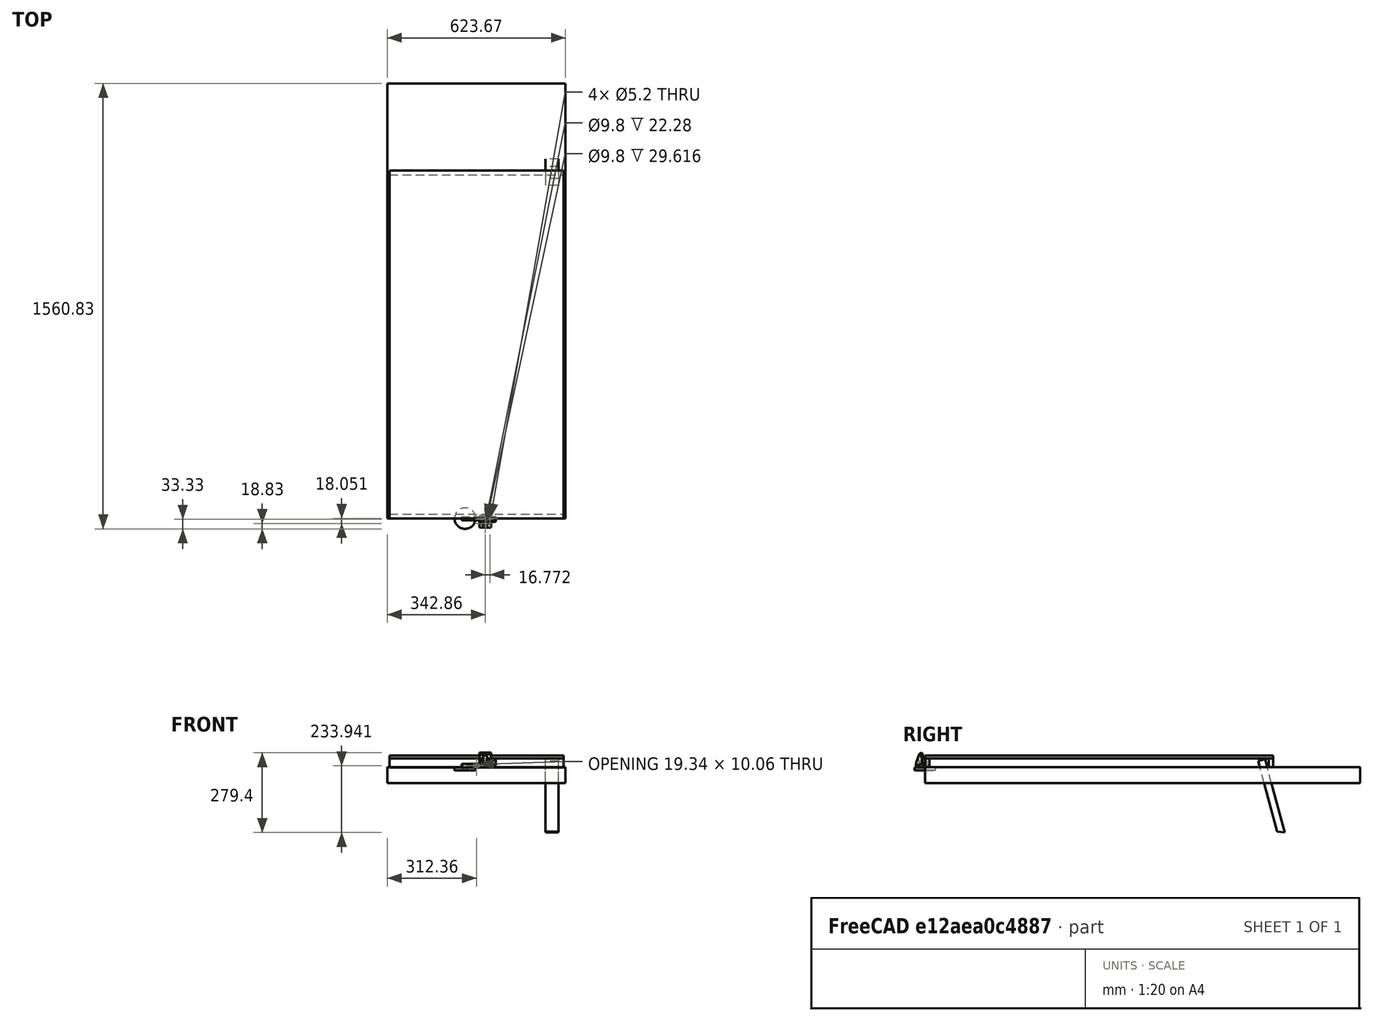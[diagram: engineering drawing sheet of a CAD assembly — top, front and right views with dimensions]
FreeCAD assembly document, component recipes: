
FREECAD ASSEMBLY — COMPONENT RECIPES ("BoardModel")

This assembly document has 4 components, labeled P0..P3 below (a component is one placed body or linked part). 4 of them carry a construction recipe — the FreeCAD feature program that regenerates the part from scratch, quoted from this document or its linked companion documents; the rest are supplied as boundary geometry only. No exploded tour is included for this assembly.
COMPONENT P0 — recipe-attached ("Board", modeled in this document).
Construction recipe (the document's own serialized feature program — sketch geometry with constraints, then the solid features built on it; lengths are millimeters unless a unit is written):

FEATURE [Sketcher::SketchObject] Sketch002
  FullyConstrained = true
  MapMode = 5
  Placement = pos=(0,0,0) rot=(0.57735,0.57735,0.57735;2.0944rad)
  Support = -> [YZ_Plane003]
  sketch-geometry (4):
    g0: LineSegment StartX=0 StartY=0 StartZ=0 EndX=15.24 EndY=0 EndZ=0
    g1: LineSegment StartX=15.24 StartY=0 StartZ=0 EndX=15.24 EndY=31.75 EndZ=0
    g2: LineSegment StartX=15.24 StartY=31.75 StartZ=0 EndX=0 EndY=31.75 EndZ=0
    g3: LineSegment StartX=0 StartY=31.75 StartZ=0 EndX=0 EndY=0 EndZ=0
  constraints (11):
    c: Coincident(g0,g1)
    c: Coincident(g1,g2)
    c: Coincident(g2,g3)
    c: Coincident(g3,g0)
    c: Horizontal(g0)
    c: Horizontal(g2)
    c: Vertical(g1)
    c: Vertical(g3)
    c: Coincident(g0,g-1)
    c: DistanceY(g3,g3) = 31.75
    c: DistanceX(g0,g0) = 15.24
FEATURE [PartDesign::Pad] Pad001
  Direction = (1,-2e-16,3e-16)
  Length = 609.6
  Length2 = 10
  Midplane = true
  Placement = pos=(0,0,0) rot=(0.57735,0.57735,0.57735;2.0944rad)
  Profile = -> Sketch002
  ReferenceAxis = -> Sketch002 [N_Axis]
  Type = 0
FEATURE [PartDesign::Body] Body002  label="Front"
  Group = -> [Sketch002,Pad001]
  Origin = -> Origin003
  Tip = -> Pad001
FEATURE [Sketcher::SketchObject] Sketch003
  AttachmentOffset = pos=(0,0,31.75) rot=(0,0,1;0rad)
  FullyConstrained = true
  MapMode = 5
  Placement = pos=(0,0,31.75) rot=(0,0,1;0rad)
  Support = -> [XY_Plane005]
  sketch-geometry (4):
    g0: LineSegment StartX=-304.8 StartY=0 StartZ=0 EndX=304.8 EndY=0 EndZ=0
    g1: LineSegment StartX=304.8 StartY=0 StartZ=0 EndX=304.8 EndY=1219.2 EndZ=0
    g2: LineSegment StartX=304.8 StartY=1219.2 StartZ=0 EndX=-304.8 EndY=1219.2 EndZ=0
    g3: LineSegment StartX=-304.8 StartY=1219.2 StartZ=0 EndX=-304.8 EndY=0 EndZ=0
  constraints (11):
    c: Coincident(g0,g1)
    c: Coincident(g1,g2)
    c: Coincident(g2,g3)
    c: Coincident(g3,g0)
    c: Horizontal(g2)
    c: Vertical(g1)
    c: Vertical(g3)
    c: Symmetric(g0,g0,g-2)
    c: DistanceX(g0,g0) = 609.6
    c: DistanceY(g3,g3) = 1219.2
    c: PointOnObject(g0,g-1)
FEATURE [PartDesign::Pad] Pad003
  Direction = (0,0,1)
  Length = 10
  Length2 = 10
  Profile = -> Sketch003
  ReferenceAxis = -> Sketch003 [N_Axis]
  Type = 0
FEATURE [PartDesign::Body] Body003  label="Top"
  Group = -> [Sketch003,Pad003]
  Origin = -> Origin005
  Tip = -> Pad003
FEATURE [Sketcher::SketchObject] Sketch013
  FullyConstrained = true
  MapMode = 5
  Placement = pos=(0,0,0) rot=(0.57735,0.57735,0.57735;2.0944rad)
  Support = -> [YZ_Plane007]
  sketch-geometry (4):
    g0: LineSegment StartX=0 StartY=0 StartZ=0 EndX=15.24 EndY=0 EndZ=0
    g1: LineSegment StartX=15.24 StartY=0 StartZ=0 EndX=15.24 EndY=31.75 EndZ=0
    g2: LineSegment StartX=15.24 StartY=31.75 StartZ=0 EndX=0 EndY=31.75 EndZ=0
    g3: LineSegment StartX=0 StartY=31.75 StartZ=0 EndX=0 EndY=0 EndZ=0
  constraints (11):
    c: Coincident(g0,g1)
    c: Coincident(g1,g2)
    c: Coincident(g2,g3)
    c: Coincident(g3,g0)
    c: Horizontal(g0)
    c: Horizontal(g2)
    c: Vertical(g1)
    c: Vertical(g3)
    c: Coincident(g0,g-1)
    c: DistanceY(g3,g3) = 31.75
    c: DistanceX(g0,g0) = 15.24
FEATURE [PartDesign::Pad] Pad007
  Direction = (1,-2e-16,3e-16)
  Length = 609.6
  Length2 = 10
  Midplane = true
  Placement = pos=(0,0,0) rot=(0.57735,0.57735,0.57735;2.0944rad)
  Profile = -> Sketch013
  ReferenceAxis = -> Sketch013 [N_Axis]
  Type = 0
FEATURE [PartDesign::Body] Body005  label="Back"
  Group = -> [Sketch013,Pad007]
  Origin = -> Origin007
  Placement = pos=(0,1204,0) rot=(0,0,1;0rad)
  Tip = -> Pad007
FEATURE [Sketcher::SketchObject] Sketch014
  FullyConstrained = true
  MapMode = 5
  Placement = pos=(0,0,0) rot=(-0.57735,0.57735,0.57735;4.18879rad)
  Support = -> [YZ_Plane008]
  sketch-geometry (4):
    g0: LineSegment StartX=-12.55 StartY=0 StartZ=0 EndX=-12.55 EndY=266.7 EndZ=0
    g1: LineSegment StartX=-12.55 StartY=0 StartZ=0 EndX=12.55 EndY=10.16 EndZ=0
    g2: LineSegment StartX=12.55 StartY=10.16 StartZ=0 EndX=12.55 EndY=266.7 EndZ=0
    g3: LineSegment StartX=-12.55 StartY=266.7 StartZ=0 EndX=12.55 EndY=266.7 EndZ=0
  constraints (11):
    c: PointOnObject(g0,g-1)
    c: Vertical(g0)
    c: Coincident(g1,g0)
    c: Coincident(g2,g1)
    c: Vertical(g2)
    c: Coincident(g3,g0)
    c: Coincident(g3,g2)
    c: Symmetric(g0,g2,g-2)
    c: DistanceY(g0,g0) = 266.7
    c: DistanceY(g2,g2) = 256.54
    c: DistanceX(g0,g1) = 25.1
FEATURE [PartDesign::Pad] Pad008
  Direction = (-1,2e-16,-3e-16)
  Length = 45
  Length2 = 10
  Placement = pos=(0,0,0) rot=(0.57735,0.57735,0.57735;2.0944rad)
  Profile = -> Sketch014
  ReferenceAxis = -> Sketch014 [N_Axis]
  Type = 0
FEATURE [PartDesign::Body] Body006  label="Leg"
  Group = -> [Sketch014,Pad008]
  Origin = -> Origin008
  Placement = pos=(287,1247.47,-230.644) rot=(1,0,0;0.261799rad)
  Tip = -> Pad008
COMPONENT P1 — recipe-attached ("FootAssembly", modeled in this document).
Construction recipe (the document's own serialized feature program — sketch geometry with constraints, then the solid features built on it; lengths are millimeters unless a unit is written):

FEATURE [Sketcher::SketchObject] Sketch
  FullyConstrained = true
  MapMode = 5
  Support = -> [XY_Plane]
  sketch-geometry (10):
    g0: LineSegment StartX=-52.3875 StartY=6.35 StartZ=0 EndX=52.3875 EndY=6.35 EndZ=0
    g1: LineSegment StartX=52.3875 StartY=6.35 StartZ=0 EndX=52.3875 EndY=-6.35 EndZ=0
    g2: LineSegment StartX=52.3875 StartY=-6.35 StartZ=0 EndX=-52.3875 EndY=-6.35 EndZ=0
    g3: LineSegment StartX=-52.3875 StartY=-6.35 StartZ=0 EndX=-52.3875 EndY=6.35 EndZ=0
    g4: Circle CenterX=-47.3875 CenterY=0 CenterZ=0 NormalX=0 NormalY=0 NormalZ=1 AngleXU=0 Radius=2.5
    g5: Circle CenterX=-32.8875 CenterY=0 CenterZ=0 NormalX=0 NormalY=0 NormalZ=1 AngleXU=0 Radius=2.5
    g6: Circle CenterX=32.8875 CenterY=0 CenterZ=0 NormalX=0 NormalY=0 NormalZ=1 AngleXU=0 Radius=2
    g7: Circle CenterX=47.3875 CenterY=0 CenterZ=0 NormalX=0 NormalY=0 NormalZ=1 AngleXU=0 Radius=2
    g8: LineSegment StartX=-47.3875 StartY=0 StartZ=0 EndX=-32.8875 EndY=0 EndZ=0
    g9: LineSegment StartX=32.8875 StartY=0 StartZ=0 EndX=47.3875 EndY=0 EndZ=0
  constraints (26):
    c: Coincident(g0,g1)
    c: Coincident(g1,g2)
    c: Coincident(g2,g3)
    c: Coincident(g3,g0)
    c: Horizontal(g2)
    c: Vertical(g1)
    c: Symmetric(g0,g0,g-2)
    c: DistanceY(g3,g3) = 12.7
    c: Symmetric(g0,g2,g-1)
    c: DistanceX(g0,g0) = 104.775
    c: PointOnObject(g4,g-1)
    c: PointOnObject(g5,g-1)
    c: PointOnObject(g6,g-1)
    c: PointOnObject(g7,g-1)
    c: Diameter(g6) = 4
    c: Equal(g7,g6)
    c: Equal(g5,g4)
    c: Coincident(g8,g4)
    c: Coincident(g8,g5)
    c: Coincident(g9,g6)
    c: Coincident(g9,g7)
    c: Equal(g9,g8)
    c: Diameter(g5) = 5
    c: DistanceX(g8,g8) = 14.5
    c: DistanceX(g0,g4) = 5
    c: DistanceX(g7,g0) = 5
FEATURE [PartDesign::Pad] Pad
  Direction = (0,0,1)
  Length = 12.7
  Length2 = 10
  Profile = -> Sketch
  ReferenceAxis = -> Sketch [N_Axis]
  Type = 0
FEATURE [Sketcher::SketchObject] Sketch001
  FullyConstrained = false
  MapMode = 5
  Support = -> [XY_Plane001]
  sketch-geometry (3):
    g0: Circle CenterX=0 CenterY=0 CenterZ=0 NormalX=0 NormalY=0 NormalZ=1 AngleXU=0 Radius=36.8321
    g1: Circle CenterX=-7.25 CenterY=0 CenterZ=0 NormalX=0 NormalY=0 NormalZ=1 AngleXU=0 Radius=2.1
    g2: Circle CenterX=7.25 CenterY=0 CenterZ=0 NormalX=0 NormalY=0 NormalZ=1 AngleXU=0 Radius=2.1
  constraints (6):
    c: Coincident(g0,g-1)
    c: PointOnObject(g1,g-1)
    c: Equal(g1,g2)
    c: Symmetric(g1,g2,g0)
    c: DistanceX(g1,g2) = 14.5
    c: Diameter(g2) = 4.2
FEATURE [PartDesign::Pad] Pad002
  Direction = (0,0,1)
  Length = 10
  Length2 = 10
  Profile = -> Sketch001
  ReferenceAxis = -> Sketch001 [N_Axis]
  Reversed = true
  Type = 0
FEATURE [Sketcher::SketchObject] Sketch004
  FullyConstrained = false
  MapMode = 5
  Placement = pos=(0,0,0) rot=(0.57735,0.57735,0.57735;2.0944rad)
  Support = -> [YZ_Plane006]
  sketch-geometry (8):
    g0: LineSegment StartX=-1.51635 StartY=-5.19268 StartZ=0 EndX=-5.92453 EndY=19.8073 EndZ=0
    g1: LineSegment StartX=12.7 StartY=8 StartZ=0 EndX=12.7 EndY=0 EndZ=0
    g2: LineSegment StartX=0 StartY=0 StartZ=0 EndX=12.7 EndY=0 EndZ=0
    g3: LineSegment StartX=12.7 StartY=8 StartZ=0 EndX=0.357421 EndY=8 EndZ=0
    g4: LineSegment StartX=0.357421 StartY=8 StartZ=0 EndX=-1.72453 EndY=19.8073 EndZ=0
    g5: LineSegment StartX=-1.72453 StartY=19.8073 StartZ=0 EndX=-5.92453 EndY=19.8073 EndZ=0
    g6: LineSegment StartX=-1.51635 StartY=-5.19268 StartZ=0 EndX=0 EndY=-5.19268 EndZ=0
    g7: LineSegment StartX=0 StartY=-5.19268 StartZ=0 EndX=0 EndY=0 EndZ=0
  constraints (21):
    c: PointOnObject(g1,g-1)
    c: Vertical(g1)
    c: Coincident(g1,g2)
    c: Angle(g-1,g0) = 1.74533
    c: DistanceY(g0,g0) = 25
    c: Coincident(g3,g1)
    c: Horizontal(g3)
    c: Coincident(g4,g3)
    c: Coincident(g5,g0)
    c: Horizontal(g5)
    c: Coincident(g6,g0)
    c: PointOnObject(g6,g-2)
    c: Horizontal(g6)
    c: Coincident(g7,g6)
    c: Coincident(g7,g2)
    c: Vertical(g7)
    c: Parallel(g4,g0)
    c: Coincident(g4,g5)
    c: DistanceY(g1,g1) = 8
    c: DistanceX(g5,g5) = 4.2
    c: DistanceX(g2,g2) = 12.7
FEATURE [PartDesign::Pad] Pad004
  Direction = (1,-2e-16,3e-16)
  Length = 55
  Length2 = 10
  Placement = pos=(0,0,0) rot=(0.57735,0.57735,0.57735;2.0944rad)
  Profile = -> Sketch004
  ReferenceAxis = -> Sketch004 [N_Axis]
  Type = 0
FEATURE [Sketcher::SketchObject] Sketch005
  AttachmentOffset = pos=(0,0,2) rot=(1,0,0;-0.174533rad)
  FullyConstrained = false
  MapMode = 5
  Placement = pos=(0,2,4e-16) rot=(0,-0.642788,-0.766044;3.14159rad)
  Support = -> [XZ_Plane006]
  sketch-geometry (5):
    g0: Circle CenterX=-44.4755 CenterY=12.9253 CenterZ=0 NormalX=0 NormalY=0 NormalZ=1 AngleXU=0 Radius=2.5
    g1: Circle CenterX=-10.5245 CenterY=12.9253 CenterZ=0 NormalX=0 NormalY=0 NormalZ=1 AngleXU=0 Radius=2.5
    g2: LineSegment StartX=-55 StartY=24.7239 StartZ=0 EndX=-55 EndY=-16.9766 EndZ=0
    g3: LineSegment StartX=-44.4755 StartY=12.9253 StartZ=0 EndX=-55 EndY=12.9253 EndZ=0
    g4: LineSegment StartX=-10.5245 StartY=12.9253 StartZ=0 EndX=0 EndY=12.9253 EndZ=0
  constraints (12):
    c: Equal(g1,g0)
    c: Horizontal(g0,g1)
    c: Vertical(g2)
    c: DistanceX(g2,g-1) = 55
    c: Coincident(g3,g0)
    c: PointOnObject(g3,g2)
    c: Horizontal(g3)
    c: Coincident(g4,g1)
    c: Horizontal(g4)
    c: PointOnObject(g4,g-2)
    c: Equal(g4,g3)
    c: Diameter(g0) = 5
FEATURE [Sketcher::SketchObject] Sketch006
  AttachmentOffset = pos=(0,0,-10) rot=(0,0,1;0rad)
  FullyConstrained = false
  MapMode = 5
  Placement = pos=(0,0,-10) rot=(0,0,1;0rad)
  Support = -> [XY_Plane001]
  sketch-geometry (3):
    g0: Circle CenterX=0 CenterY=0 CenterZ=0 NormalX=0 NormalY=0 NormalZ=1 AngleXU=0 Radius=36.8321
    g1: Circle CenterX=-7.25 CenterY=0 CenterZ=0 NormalX=0 NormalY=0 NormalZ=1 AngleXU=0 Radius=3.75
    g2: Circle CenterX=7.25 CenterY=0 CenterZ=0 NormalX=0 NormalY=0 NormalZ=1 AngleXU=0 Radius=3.75
  constraints (6):
    c: Coincident(g0,g-1)
    c: PointOnObject(g1,g-1)
    c: Equal(g1,g2)
    c: Symmetric(g1,g2,g0)
    c: DistanceX(g1,g2) = 14.5
    c: Diameter(g2) = 7.5
FEATURE [PartDesign::Pocket] Pocket001
  BaseFeature = -> Pad002
  Direction = (0,0,-1)
  Length = 5
  Length2 = 5
  Profile = -> Sketch006
  ReferenceAxis = -> Sketch006 [N_Axis]
  Reversed = true
  Type = 0
FEATURE [PartDesign::Body] Body001  label="Foot"
  Group = -> [Sketch001,Pad002,Sketch006,Pocket001]
  Origin = -> Origin001
  Placement = pos=(-40.005,0,0) rot=(0,0,1;0rad)
  Tip = -> Pocket001
FEATURE [Sketcher::SketchObject] Sketch007
  FullyConstrained = false
  MapMode = 5
  Support = -> [XY_Plane006]
  sketch-geometry (6):
    g0: Circle CenterX=20.25 CenterY=6.35 CenterZ=0 NormalX=0 NormalY=0 NormalZ=1 AngleXU=0 Radius=2.6
    g1: Circle CenterX=34.75 CenterY=6.35 CenterZ=0 NormalX=0 NormalY=0 NormalZ=1 AngleXU=0 Radius=2.6
    g2: LineSegment StartX=40.5 StartY=12.7 StartZ=0 EndX=35.9057 EndY=12.7 EndZ=0
    g3: LineSegment StartX=20.25 StartY=6.35 StartZ=0 EndX=34.75 EndY=6.35 EndZ=0
    g4: LineSegment StartX=55 StartY=10.9102 StartZ=0 EndX=55 EndY=0 EndZ=0
    g5: LineSegment StartX=27.5 StartY=6.35 StartZ=0 EndX=27.5 EndY=0 EndZ=0
  constraints (15):
    c: Horizontal(g1,g0)
    c: Equal(g1,g0)
    c: DistanceX(g0,g1) = 14.5
    c: Diameter(g1) = 5.2
    c: Horizontal(g2)
    c: DistanceY(g-1,g2) = 12.7
    c: Coincident(g3,g0)
    c: Coincident(g3,g1)
    c: Symmetric(g2,g-1,g0)
    c: PointOnObject(g4,g-1)
    c: Vertical(g4)
    c: DistanceX(g-1,g4) = 55
    c: Vertical(g5)
    c: Symmetric(g-1,g4,g5)
    c: Symmetric(g0,g1,g5)
FEATURE [PartDesign::Pocket] Pocket
  BaseFeature = -> Pad004
  Direction = (0,0,-1)
  Length = 10
  Length2 = 5
  Placement = pos=(0,0,0) rot=(0.57735,0.57735,0.57735;2.0944rad)
  Profile = -> Sketch007
  ReferenceAxis = -> Sketch007 [N_Axis]
  Reversed = true
  Type = 0
FEATURE [PartDesign::Pocket] Pocket002
  BaseFeature = -> Pocket
  Direction = (0,-0.984808,-0.173648)
  Length = 5
  Length2 = 5
  Placement = pos=(0,0,0) rot=(0.57735,0.57735,0.57735;2.0944rad)
  Profile = -> Sketch005
  ReferenceAxis = -> Sketch005 [N_Axis]
  Type = 0
FEATURE [Sketcher::SketchObject] Sketch008
  AttachmentOffset = pos=(0,0,4) rot=(0,0,1;0rad)
  FullyConstrained = false
  MapMode = 5
  Placement = pos=(0,0,4) rot=(0,0,1;0rad)
  Support = -> [XY_Plane006]
  sketch-geometry (6):
    g0: Circle CenterX=20.25 CenterY=6.35 CenterZ=0 NormalX=0 NormalY=0 NormalZ=1 AngleXU=0 Radius=4.4
    g1: Circle CenterX=34.75 CenterY=6.35 CenterZ=0 NormalX=0 NormalY=0 NormalZ=1 AngleXU=0 Radius=4.4
    g2: LineSegment StartX=40.5 StartY=12.7 StartZ=0 EndX=35.9057 EndY=12.7 EndZ=0
    g3: LineSegment StartX=20.25 StartY=6.35 StartZ=0 EndX=34.75 EndY=6.35 EndZ=0
    g4: LineSegment StartX=55 StartY=10.9102 StartZ=0 EndX=55 EndY=0 EndZ=0
    g5: LineSegment StartX=27.5 StartY=6.35 StartZ=0 EndX=27.5 EndY=0 EndZ=0
  constraints (15):
    c: Horizontal(g1,g0)
    c: Equal(g1,g0)
    c: DistanceX(g0,g1) = 14.5
    c: Diameter(g1) = 8.8
    c: Horizontal(g2)
    c: DistanceY(g-1,g2) = 12.7
    c: Coincident(g3,g0)
    c: Coincident(g3,g1)
    c: Symmetric(g2,g-1,g0)
    c: PointOnObject(g4,g-1)
    c: Vertical(g4)
    c: DistanceX(g-1,g4) = 55
    c: Vertical(g5)
    c: Symmetric(g-1,g4,g5)
    c: Symmetric(g0,g1,g5)
FEATURE [PartDesign::Pocket] Pocket003
  BaseFeature = -> Pocket002
  Direction = (0,0,-1)
  Length = 5
  Length2 = 5
  Placement = pos=(0,0,0) rot=(0.57735,0.57735,0.57735;2.0944rad)
  Profile = -> Sketch008
  ReferenceAxis = -> Sketch008 [N_Axis]
  Reversed = true
  Type = 0
FEATURE [Sketcher::SketchObject] Sketch009
  FullyConstrained = false
  MapMode = 5
  Placement = pos=(0,0,0) rot=(0.57735,0.57735,0.57735;2.0944rad)
  Support = -> [YZ_Plane006]
  sketch-geometry (11):
    g0: LineSegment StartX=-1.51635 StartY=-5.19267 StartZ=0 EndX=-5.92453 EndY=19.8073 EndZ=0
    g1: LineSegment StartX=12.7 StartY=8 StartZ=0 EndX=12.7 EndY=0 EndZ=0
    g2: LineSegment StartX=0 StartY=0 StartZ=0 EndX=12.7 EndY=0 EndZ=0
    g3: LineSegment StartX=12.7 StartY=8 StartZ=0 EndX=0.357421 EndY=8 EndZ=0
    g4: LineSegment StartX=0.357421 StartY=8 StartZ=0 EndX=-1.72453 EndY=19.8073 EndZ=0
    g5: LineSegment StartX=-1.72453 StartY=19.8073 StartZ=0 EndX=-5.92453 EndY=19.8073 EndZ=0
    g6: LineSegment StartX=-1.51635 StartY=-5.19267 StartZ=0 EndX=0 EndY=-5.19267 EndZ=0
    g7: LineSegment StartX=0 StartY=-5.19267 StartZ=0 EndX=0 EndY=0 EndZ=0
    g8: LineSegment StartX=-1.72453 StartY=19.8073 StartZ=0 EndX=2.33774 EndY=19.8073 EndZ=0
    g9: LineSegment StartX=12.7 StartY=9.44507 StartZ=0 EndX=12.7 EndY=8 EndZ=0
    g10: ArcOfCircle CenterX=2.33774 CenterY=9.44507 CenterZ=0 NormalX=0 NormalY=0 NormalZ=1 AngleXU=0 Radius=10.3623 StartAngle=0 EndAngle=1.5708
  constraints (29):
    c: PointOnObject(g1,g-1)
    c: Vertical(g1)
    c: Coincident(g1,g2)
    c: Angle(g-1,g0) = 1.74533
    c: DistanceY(g0,g0) = 25
    c: Coincident(g3,g1)
    c: Horizontal(g3)
    c: Coincident(g4,g3)
    c: Coincident(g5,g0)
    c: Horizontal(g5)
    c: Coincident(g6,g0)
    c: PointOnObject(g6,g-2)
    c: Horizontal(g6)
    c: Coincident(g7,g6)
    c: Coincident(g7,g2)
    c: Vertical(g7)
    c: Parallel(g4,g0)
    c: Coincident(g4,g5)
    c: DistanceY(g1,g1) = 8
    c: DistanceX(g5,g5) = 4.2
    c: DistanceX(g2,g2) = 12.7
    c: DistanceX(g3) = 0.357421
    c: DistanceX(g4) = -1.72453
    c: Coincident(g8,g4)
    c: Horizontal(g8)
    c: Coincident(g9,g1)
    c: Vertical(g9)
    c: Tangent(g8,g10) = 1.5708
    c: Tangent(g9,g10) = 1.5708
FEATURE [PartDesign::Pad] Pad005
  BaseFeature = -> Pocket003
  Direction = (1,-2e-16,3e-16)
  Length = 4
  Length2 = 10
  Placement = pos=(0,0,0) rot=(0.57735,0.57735,0.57735;2.0944rad)
  Profile = -> Sketch009
  ReferenceAxis = -> Sketch009 [N_Axis]
  Type = 0
FEATURE [Sketcher::SketchObject] Sketch010
  AttachmentOffset = pos=(0,0,55) rot=(0,0,1;0rad)
  FullyConstrained = false
  MapMode = 5
  Placement = pos=(55,-1.22e-14,1.22e-14) rot=(0.57735,0.57735,0.57735;2.0944rad)
  Support = -> [YZ_Plane006]
  sketch-geometry (11):
    g0: LineSegment StartX=-1.51635 StartY=-5.19267 StartZ=0 EndX=-5.92453 EndY=19.8073 EndZ=0
    g1: LineSegment StartX=12.7 StartY=8 StartZ=0 EndX=12.7 EndY=0 EndZ=0
    g2: LineSegment StartX=0 StartY=0 StartZ=0 EndX=12.7 EndY=0 EndZ=0
    g3: LineSegment StartX=12.7 StartY=8 StartZ=0 EndX=0.357421 EndY=8 EndZ=0
    g4: LineSegment StartX=0.357421 StartY=8 StartZ=0 EndX=-1.72453 EndY=19.8073 EndZ=0
    g5: LineSegment StartX=-1.72453 StartY=19.8073 StartZ=0 EndX=-5.92453 EndY=19.8073 EndZ=0
    g6: LineSegment StartX=-1.51635 StartY=-5.19267 StartZ=0 EndX=0 EndY=-5.19267 EndZ=0
    g7: LineSegment StartX=0 StartY=-5.19267 StartZ=0 EndX=0 EndY=0 EndZ=0
    g8: LineSegment StartX=-1.72453 StartY=19.8073 StartZ=0 EndX=2.33774 EndY=19.8073 EndZ=0
    g9: LineSegment StartX=12.7 StartY=9.44507 StartZ=0 EndX=12.7 EndY=8 EndZ=0
    g10: ArcOfCircle CenterX=2.33774 CenterY=9.44507 CenterZ=0 NormalX=0 NormalY=0 NormalZ=1 AngleXU=0 Radius=10.3623 StartAngle=0 EndAngle=1.5708
  constraints (29):
    c: PointOnObject(g1,g-1)
    c: Vertical(g1)
    c: Coincident(g1,g2)
    c: Angle(g-1,g0) = 1.74533
    c: DistanceY(g0,g0) = 25
    c: Coincident(g3,g1)
    c: Horizontal(g3)
    c: Coincident(g4,g3)
    c: Coincident(g5,g0)
    c: Horizontal(g5)
    c: Coincident(g6,g0)
    c: PointOnObject(g6,g-2)
    c: Horizontal(g6)
    c: Coincident(g7,g6)
    c: Coincident(g7,g2)
    c: Vertical(g7)
    c: Parallel(g4,g0)
    c: Coincident(g4,g5)
    c: DistanceY(g1,g1) = 8
    c: DistanceX(g5,g5) = 4.2
    c: DistanceX(g2,g2) = 12.7
    c: DistanceX(g3) = 0.357421
    c: DistanceX(g4) = -1.72453
    c: Coincident(g8,g4)
    c: Horizontal(g8)
    c: Coincident(g9,g1)
    c: Vertical(g9)
    c: Tangent(g8,g10) = 1.5708
    c: Tangent(g9,g10) = 1.5708
FEATURE [PartDesign::Pad] Pad006
  BaseFeature = -> Pad005
  Direction = (1,-2e-16,3e-16)
  Length = 4
  Length2 = 10
  Placement = pos=(0,0,0) rot=(0.57735,0.57735,0.57735;2.0944rad)
  Profile = -> Sketch010
  ReferenceAxis = -> Sketch010 [N_Axis]
  Reversed = true
  Type = 0
FEATURE [Sketcher::SketchObject] Sketch011
  FullyConstrained = false
  MapMode = 5
  Placement = pos=(0,0,0) rot=(1,0,0;1.5708rad)
  Support = -> [XZ_Plane]
  sketch-geometry (2):
    g0: ArcOfCircle CenterX=-4.4394 CenterY=6.54104 CenterZ=0 NormalX=0 NormalY=0 NormalZ=1 AngleXU=0 Radius=5.22923 StartAngle=0.556784 EndAngle=5.7264
    g1: ArcOfCircle CenterX=4.4394 CenterY=6.54104 CenterZ=0 NormalX=0 NormalY=0 NormalZ=1 AngleXU=0 Radius=5.22923 StartAngle=3.69838 EndAngle=8.86799
  constraints (5):
    c: Equal(g1,g0)
    c: Vertical(g0,g0)
    c: Vertical(g1,g1)
    c: Symmetric(g1,g0,g-2)
    c: Coincident(g0,g1)
FEATURE [PartDesign::Pocket] Pocket004
  BaseFeature = -> Pad
  Direction = (0,1,2e-16)
  Length = 5
  Length2 = 5
  Midplane = true
  Profile = -> Sketch011
  ReferenceAxis = -> Sketch011 [N_Axis]
  Type = 1
FEATURE [PartDesign::Body] Body  label="Loadcell"
  Group = -> [Sketch,Pad,Sketch011,Pocket004]
  Origin = -> Origin
  Tip = -> Pocket004
FEATURE [Sketcher::SketchObject] Sketch012
  ExternalGeometry = -> [Pad006]
  FullyConstrained = false
  MapMode = 5
  Placement = pos=(5.6e-15,12.7,-2.8e-15) rot=(0.57735,0.57735,0.57735;4.18879rad)
  Support = -> [Pad006]
  sketch-geometry (10):
    g0: LineSegment StartX=0 StartY=43.1845 StartZ=0 EndX=3.04874 EndY=43.1845 EndZ=0
    g1: LineSegment StartX=3.04874 StartY=55 StartZ=0 EndX=-3.04704 EndY=55 EndZ=0
    g2: LineSegment StartX=-3.04704 StartY=55 StartZ=0 EndX=-3.04704 EndY=0 EndZ=0
    g3: LineSegment StartX=-3.04704 StartY=0 StartZ=0 EndX=0 EndY=0 EndZ=0
    g4: LineSegment StartX=0 StartY=0 StartZ=0 EndX=3.04874 EndY=0 EndZ=0
    g5: LineSegment StartX=3.04874 StartY=0 StartZ=0 EndX=3.04874 EndY=11.8155 EndZ=0
    g6: LineSegment StartX=3.04874 StartY=11.8155 StartZ=0 EndX=0 EndY=11.8155 EndZ=0
    g7: LineSegment StartX=0 StartY=11.8155 StartZ=0 EndX=0 EndY=43.1845 EndZ=0
    g8: LineSegment StartX=-3.04704 StartY=27.5 StartZ=0 EndX=7.44408 EndY=27.5 EndZ=0
    g9: LineSegment StartX=3.04874 StartY=55 StartZ=0 EndX=3.04874 EndY=43.1845 EndZ=0
  constraints (24):
    c: PointOnObject(g0,g-2)
    c: Horizontal(g0)
    c: Horizontal(g1)
    c: Coincident(g2,g1)
    c: PointOnObject(g2,g-1)
    c: Vertical(g2)
    c: Coincident(g3,g2)
    c: Coincident(g3,g-1)
    c: Coincident(g4,g3)
    c: PointOnObject(g4,g-1)
    c: Coincident(g5,g4)
    c: Vertical(g5)
    c: Coincident(g6,g5)
    c: Horizontal(g6)
    c: PointOnObject(g6,g-2)
    c: Coincident(g7,g6)
    c: Coincident(g7,g0)
    c: Equal(g0,g6)
    c: Symmetric(g1,g2,g8)
    c: Symmetric(g0,g5,g8)
    c: Coincident(g9,g1)
    c: Coincident(g9,g0)
    c: Vertical(g9)
    c: PointOnObject(g1,g-3)
FEATURE [PartDesign::Pocket] Pocket005
  BaseFeature = -> Pad006
  Direction = (-8e-16,-1,1e-16)
  Length = 0
  Length2 = 5
  Placement = pos=(0,0,0) rot=(0.57735,0.57735,0.57735;2.0944rad)
  Profile = -> Sketch012
  ReferenceAxis = -> Sketch012 [N_Axis]
  Type = 3
  UpToFace = -> Pad006 [Face8]
FEATURE [PartDesign::Body] Body004  label="Mnt"
  Group = -> [Sketch004,Pad004,Sketch005,Sketch007,Pocket,Pocket002,Sketch008,Pocket003,Sketch009,Pad005,Sketch010,Pad006,Sketch012,Pocket005]
  Origin = -> Origin006
  Placement = pos=(12.5222,-6.2992,12.7254) rot=(0,0,1;0rad)
  Tip = -> Pocket005
COMPONENT P2 — recipe-attached ("Floor", modeled in this document).
Construction recipe (the document's own serialized feature program — sketch geometry with constraints, then the solid features built on it; lengths are millimeters unless a unit is written):

FEATURE [Sketcher::SketchObject] Sketch015
  FullyConstrained = false
  MapMode = 5
  Placement = pos=(0,0,0) rot=(1,0,0;1.5708rad)
  Support = -> [XZ_Plane010]
  sketch-geometry (4):
    g0: LineSegment StartX=-312.359 StartY=1.62053 StartZ=0 EndX=311.309 EndY=1.62053 EndZ=0
    g1: LineSegment StartX=311.309 StartY=1.62053 StartZ=0 EndX=311.309 EndY=-54.3871 EndZ=0
    g2: LineSegment StartX=311.309 StartY=-54.3871 StartZ=0 EndX=-312.359 EndY=-54.3871 EndZ=0
    g3: LineSegment StartX=-312.359 StartY=-54.3871 StartZ=0 EndX=-312.359 EndY=1.62053 EndZ=0
  constraints (8):
    c: Coincident(g0,g1)
    c: Coincident(g1,g2)
    c: Coincident(g2,g3)
    c: Coincident(g3,g0)
    c: Horizontal(g0)
    c: Horizontal(g2)
    c: Vertical(g1)
    c: Vertical(g3)
FEATURE [PartDesign::Pad] Pad009
  Direction = (0,-1,2e-16)
  Length = 1524
  Length2 = 10
  Placement = pos=(0,0,0) rot=(1,0,0;1.5708rad)
  Profile = -> Sketch015
  ReferenceAxis = -> Sketch015 [N_Axis]
  Reversed = true
  Type = 0
FEATURE [PartDesign::Body] Body007
  Group = -> [Sketch015,Pad009]
  Origin = -> Origin010
  Tip = -> Pad009
COMPONENT P3 — recipe-attached ("RearFoot", modeled in this document).
Construction recipe (the document's own serialized feature program — sketch geometry with constraints, then the solid features built on it; lengths are millimeters unless a unit is written):

FEATURE [Sketcher::SketchObject] Sketch016
  FullyConstrained = false
  MapMode = 5
  Placement = pos=(0,0,0) rot=(0.57735,0.57735,0.57735;2.0944rad)
  Support = -> [YZ_Plane013]
  sketch-geometry (11):
    g0: LineSegment StartX=23.3154 StartY=0 StartZ=0 EndX=0 EndY=50 EndZ=0
    g1: LineSegment StartX=0 StartY=50 StartZ=0 EndX=-9.06308 EndY=45.7738 EndZ=0
    g2: LineSegment StartX=-6 StartY=25.3407 StartZ=0 EndX=-6 EndY=0 EndZ=0
    g3: LineSegment StartX=8.5 StartY=25.3407 StartZ=0 EndX=8.5 EndY=0 EndZ=0
    g4: LineSegment StartX=-10.9 StartY=20 StartZ=0 EndX=-1.1 EndY=20 EndZ=0
    g5: LineSegment StartX=3.6 StartY=20 StartZ=0 EndX=13.4 EndY=20 EndZ=0
    g6: LineSegment StartX=23.3154 StartY=0 StartZ=0 EndX=-20 EndY=0 EndZ=0
    g7: LineSegment StartX=-20 StartY=0 StartZ=0 EndX=-20 EndY=12 EndZ=0
    g8: LineSegment StartX=-26.8019 StartY=10.8 StartZ=0 EndX=-14.4043 EndY=10.8 EndZ=0
    g9: LineSegment StartX=-20 StartY=12 StartZ=0 EndX=-9.06308 EndY=45.7738 EndZ=0
    g10: LineSegment StartX=13.75 StartY=0 StartZ=0 EndX=13.75 EndY=10.7671 EndZ=0
  constraints (33):
    c: PointOnObject(g0,g-1)
    c: Coincident(g1,g0)
    c: Vertical(g2)
    c: Vertical(g3)
    c: DistanceX(g2,g3) = 14.5
    c: Horizontal(g3,g2)
    c: Horizontal(g2,g3)
    c: DistanceY(g2,g4) = 20
    c: Symmetric(g4,g4,g2)
    c: Symmetric(g5,g5,g3)
    c: Horizontal(g4,g5)
    c: DistanceY(g-1,g0) = 50
    c: Distance(g1) = 10
    c: PointOnObject(g0,g-2)
    c: Coincident(g6,g0)
    c: PointOnObject(g6,g-1)
    c: Coincident(g7,g6)
    c: Vertical(g7)
    c: DistanceX(g6,g-1) = 20
    c: Equal(g5,g4)
    c: Horizontal(g8)
    c: Coincident(g9,g7)
    c: Coincident(g9,g1)
    c: Angle(g-2,g0) = 0.436332
    c: Perpendicular(g0,g1)
    c: DistanceY(g6,g7) = 12
    c: DistanceX(g5,g5) = 9.8
    c: DistanceY(g-1,g5) = 20
    c: DistanceX(g-1,g3) = 8.5
    c: PointOnObject(g10,g6)
    c: Vertical(g10)
    c: DistanceX(g6,g10) = 33.75
    c: DistanceY(g6,g8) = 10.8
FEATURE [PartDesign::Pad] Pad010
  Direction = (1,-2e-16,3e-16)
  Length = 40
  Length2 = 10
  Midplane = true
  Placement = pos=(0,0,0) rot=(0.57735,0.57735,0.57735;2.0944rad)
  Profile = -> Sketch016
  ReferenceAxis = -> Sketch016 [N_Axis]
  Type = 0
FEATURE [Sketcher::SketchObject] Sketch017  label="CounterBore"
  AttachmentOffset = pos=(0,0,20) rot=(0,0,1;0rad)
  FullyConstrained = true
  MapMode = 5
  Placement = pos=(0,0,20) rot=(0,0,1;0rad)
  Support = -> [XY_Plane013]
  sketch-geometry (2):
    g0: Circle CenterX=0 CenterY=-6 CenterZ=0 NormalX=0 NormalY=0 NormalZ=1 AngleXU=0 Radius=4.9
    g1: Circle CenterX=0 CenterY=8.5 CenterZ=0 NormalX=0 NormalY=0 NormalZ=1 AngleXU=0 Radius=4.9
  constraints (6):
    c: PointOnObject(g0,g-2)
    c: PointOnObject(g1,g-2)
    c: Equal(g1,g0)
    c: Diameter(g1) = 9.8
    c: DistanceY(g0,g1) = 14.5
    c: DistanceY(g-1,g1) = 8.5
FEATURE [Sketcher::SketchObject] Sketch018
  AttachmentOffset = pos=(0,0,20) rot=(0,0,1;0rad)
  FullyConstrained = true
  MapMode = 5
  Placement = pos=(0,-20,-4.4e-15) rot=(1,0,0;1.5708rad)
  Support = -> [XZ_Plane013]
  sketch-geometry (4):
    g0: LineSegment StartX=-6.375 StartY=0 StartZ=0 EndX=6.375 EndY=0 EndZ=0
    g1: LineSegment StartX=6.375 StartY=0 StartZ=0 EndX=6.375 EndY=10.8 EndZ=0
    g2: LineSegment StartX=6.375 StartY=10.8 StartZ=0 EndX=-6.375 EndY=10.8 EndZ=0
    g3: LineSegment StartX=-6.375 StartY=10.8 StartZ=0 EndX=-6.375 EndY=0 EndZ=0
  constraints (11):
    c: Coincident(g0,g1)
    c: Coincident(g1,g2)
    c: Coincident(g2,g3)
    c: Coincident(g3,g0)
    c: Horizontal(g2)
    c: Vertical(g1)
    c: Vertical(g3)
    c: PointOnObject(g0,g-1)
    c: Symmetric(g0,g0,g-2)
    c: DistanceX(g0,g0) = 12.75
    c: DistanceY(g0,g1) = 10.8
FEATURE [PartDesign::Pocket] Pocket006
  BaseFeature = -> Pad010
  Direction = (0,1,-2e-16)
  Length = 33.75
  Length2 = 5
  Placement = pos=(0,0,0) rot=(0.57735,0.57735,0.57735;2.0944rad)
  Profile = -> Sketch018
  ReferenceAxis = -> Sketch018 [N_Axis]
  Type = 0
FEATURE [Sketcher::SketchObject] Sketch019
  AttachmentOffset = pos=(0,5,-13) rot=(1,0,0;0.436332rad)
  FullyConstrained = false
  MapMode = 5
  Placement = pos=(0,13,5) rot=(1,0,0;2.00713rad)
  Support = -> [XZ_Plane013]
  sketch-geometry (10):
    g0: LineSegment StartX=-29.4073 StartY=60.2052 StartZ=0 EndX=-7 EndY=60.2052 EndZ=0
    g1: LineSegment StartX=-7 StartY=60.2052 StartZ=0 EndX=-7 EndY=24.8017 EndZ=0
    g2: LineSegment StartX=-19.8017 StartY=12 StartZ=0 EndX=-29.4073 EndY=12 EndZ=0
    g3: LineSegment StartX=-29.4073 StartY=12 StartZ=0 EndX=-29.4073 EndY=60.2052 EndZ=0
    g4: LineSegment StartX=7 StartY=60.2052 StartZ=0 EndX=29.4073 EndY=60.2052 EndZ=0
    g5: LineSegment StartX=29.4073 StartY=60.2052 StartZ=0 EndX=29.4073 EndY=12 EndZ=0
    g6: LineSegment StartX=29.4073 StartY=12 StartZ=0 EndX=19.8017 EndY=12 EndZ=0
    g7: LineSegment StartX=7 StartY=24.8017 StartZ=0 EndX=7 EndY=60.2052 EndZ=0
    g8: ArcOfCircle CenterX=-19.8017 CenterY=24.8017 CenterZ=0 NormalX=0 NormalY=0 NormalZ=1 AngleXU=0 Radius=12.8017 StartAngle=4.71239 EndAngle=6.28319
    g9: ArcOfCircle CenterX=19.8017 CenterY=24.8017 CenterZ=0 NormalX=0 NormalY=0 NormalZ=1 AngleXU=0 Radius=12.8017 StartAngle=3.14159 EndAngle=4.71239
  constraints (23):
    c: Coincident(g0,g1)
    c: Coincident(g2,g3)
    c: Coincident(g3,g0)
    c: Horizontal(g0)
    c: Horizontal(g2)
    c: Vertical(g1)
    c: Vertical(g3)
    c: Coincident(g4,g5)
    c: Coincident(g5,g6)
    c: Coincident(g7,g4)
    c: Horizontal(g4)
    c: Horizontal(g6)
    c: Vertical(g5)
    c: Vertical(g7)
    c: Tangent(g2,g8) = 1.5708
    c: Tangent(g1,g8) = 1.5708
    c: Tangent(g7,g9) = 1.5708
    c: Tangent(g6,g9) = 1.5708
    c: Horizontal(g6,g2)
    c: Symmetric(g7,g1,g-2)
    c: Symmetric(g0,g4,g-2)
    c: DistanceY(g-1,g2) = 12
    c: DistanceX(g1,g7) = 14
FEATURE [PartDesign::Pocket] Pocket007
  BaseFeature = -> Pocket006
  Direction = (0,0.906308,0.422618)
  Length = 50
  Length2 = 5
  Placement = pos=(0,0,0) rot=(0.57735,0.57735,0.57735;2.0944rad)
  Profile = -> Sketch019
  ReferenceAxis = -> Sketch019 [N_Axis]
  Reversed = true
  Type = 0
FEATURE [PartDesign::Pocket] Pocket008
  BaseFeature = -> Pocket007
  Direction = (0,0,-1)
  Length = 30
  Length2 = 5
  Placement = pos=(0,0,0) rot=(0.57735,0.57735,0.57735;2.0944rad)
  Profile = -> Sketch017
  ReferenceAxis = -> Sketch017 [N_Axis]
  Reversed = true
  Type = 1
FEATURE [Sketcher::SketchObject] Sketch020  label="BoltHoles"
  AttachmentOffset = pos=(0,0,20) rot=(0,0,1;0rad)
  FullyConstrained = true
  MapMode = 5
  Placement = pos=(0,0,20) rot=(0,0,1;0rad)
  Support = -> [XY_Plane013]
  sketch-geometry (2):
    g0: Circle CenterX=0 CenterY=-6 CenterZ=0 NormalX=0 NormalY=0 NormalZ=1 AngleXU=0 Radius=2.6
    g1: Circle CenterX=0 CenterY=8.5 CenterZ=0 NormalX=0 NormalY=0 NormalZ=1 AngleXU=0 Radius=2.6
  constraints (6):
    c: PointOnObject(g0,g-2)
    c: PointOnObject(g1,g-2)
    c: Equal(g1,g0)
    c: Diameter(g1) = 5.2
    c: DistanceY(g0,g1) = 14.5
    c: DistanceY(g-1,g1) = 8.5
FEATURE [PartDesign::Pocket] Pocket009
  BaseFeature = -> Pocket008
  Direction = (0,0,-1)
  Length = 5
  Length2 = 5
  Placement = pos=(0,0,0) rot=(0.57735,0.57735,0.57735;2.0944rad)
  Profile = -> Sketch020
  ReferenceAxis = -> Sketch020 [N_Axis]
  Type = 1
FEATURE [Sketcher::SketchObject] Sketch021
  AttachmentOffset = pos=(0,5,-10) rot=(1,0,0;0.436332rad)
  FullyConstrained = false
  MapMode = 5
  Placement = pos=(0,10,5) rot=(1,0,0;2.00713rad)
  Support = -> [XZ_Plane013]
  sketch-geometry (6):
    g0: Circle CenterX=15.5 CenterY=18.346 CenterZ=0 NormalX=0 NormalY=0 NormalZ=1 AngleXU=0 Radius=2.5
    g1: Circle CenterX=-15.5 CenterY=18.346 CenterZ=0 NormalX=0 NormalY=0 NormalZ=1 AngleXU=0 Radius=2.5
    g2: Circle CenterX=15.5 CenterY=40.846 CenterZ=0 NormalX=0 NormalY=0 NormalZ=1 AngleXU=0 Radius=2.5
    g3: Circle CenterX=-15.5 CenterY=40.846 CenterZ=0 NormalX=0 NormalY=0 NormalZ=1 AngleXU=0 Radius=2.5
    g4: Circle CenterX=-15.5 CenterY=18.346 CenterZ=0 NormalX=0 NormalY=0 NormalZ=1 AngleXU=0 Radius=5.75
    g5: Circle CenterX=15.5 CenterY=18.346 CenterZ=0 NormalX=0 NormalY=0 NormalZ=1 AngleXU=0 Radius=5.75
  constraints (13):
    c: Equal(g3,g1)
    c: Equal(g1,g0)
    c: Equal(g0,g2)
    c: Symmetric(g1,g0,g-2)
    c: Symmetric(g3,g2,g-2)
    c: Vertical(g3,g1)
    c: Coincident(g4,g1)
    c: Coincident(g5,g0)
    c: Diameter(g4) = 11.5
    c: Equal(g4,g5)
    c: DistanceX(g1,g-1) = 15.5
    c: DistanceY(g1,g3) = 22.5
    c: Diameter(g1) = 5
FEATURE [PartDesign::Pocket] Pocket010
  BaseFeature = -> Pocket009
  Direction = (0,0.906308,0.422618)
  Length = 5
  Length2 = 5
  Placement = pos=(0,0,0) rot=(0.57735,0.57735,0.57735;2.0944rad)
  Profile = -> Sketch021
  ReferenceAxis = -> Sketch021 [N_Axis]
  Type = 1
FEATURE [Sketcher::SketchObject] Sketch022
  FullyConstrained = false
  MapMode = 5
  Support = -> [XY_Plane013]
  sketch-geometry (4):
    g0: LineSegment StartX=-7.9 StartY=-20.1143 StartZ=0 EndX=7.9 EndY=-20.1143 EndZ=0
    g1: LineSegment StartX=7.9 StartY=-20.1143 StartZ=0 EndX=7.37717 EndY=-2.31433 EndZ=0
    g2: LineSegment StartX=7.37717 StartY=-2.31433 StartZ=0 EndX=-7.37717 EndY=-2.31433 EndZ=0
    g3: LineSegment StartX=-7.37717 StartY=-2.31433 StartZ=0 EndX=-7.9 EndY=-20.1143 EndZ=0
  constraints (8):
    c: Coincident(g0,g1)
    c: Coincident(g1,g2)
    c: Coincident(g2,g3)
    c: Coincident(g3,g0)
    c: Symmetric(g0,g0,g-2)
    c: DistanceX(g0,g0) = 15.8
    c: Symmetric(g2,g1,g-2)
    c: DistanceY(g0,g2) = 17.8
FEATURE [PartDesign::Pocket] Pocket011
  BaseFeature = -> Pocket010
  Direction = (0,0,-1)
  Length = 11
  Length2 = 5
  Placement = pos=(0,0,0) rot=(0.57735,0.57735,0.57735;2.0944rad)
  Profile = -> Sketch022
  ReferenceAxis = -> Sketch022 [N_Axis]
  Reversed = true
  Type = 2
FEATURE [PartDesign::Body] Body009  label="RearMnt"
  Group = -> [Sketch016,Pad010,Sketch017,Sketch018,Pocket006,Sketch019,Pocket007,Pocket008,Sketch020,Pocket009,Sketch021,Pocket010,Sketch022,Pocket011]
  Origin = -> Origin013
  Placement = pos=(30.5,-12,2) rot=(0,0,1;0rad)
  Tip = -> Pocket011
PROVENANCE & LICENSES
A FreeCAD (.FCStd) document from a public repository crawl; recipes are the document's own serialized feature recipes (and, for linked parts, companion documents' recipes).
License: lgpl-3.0.
